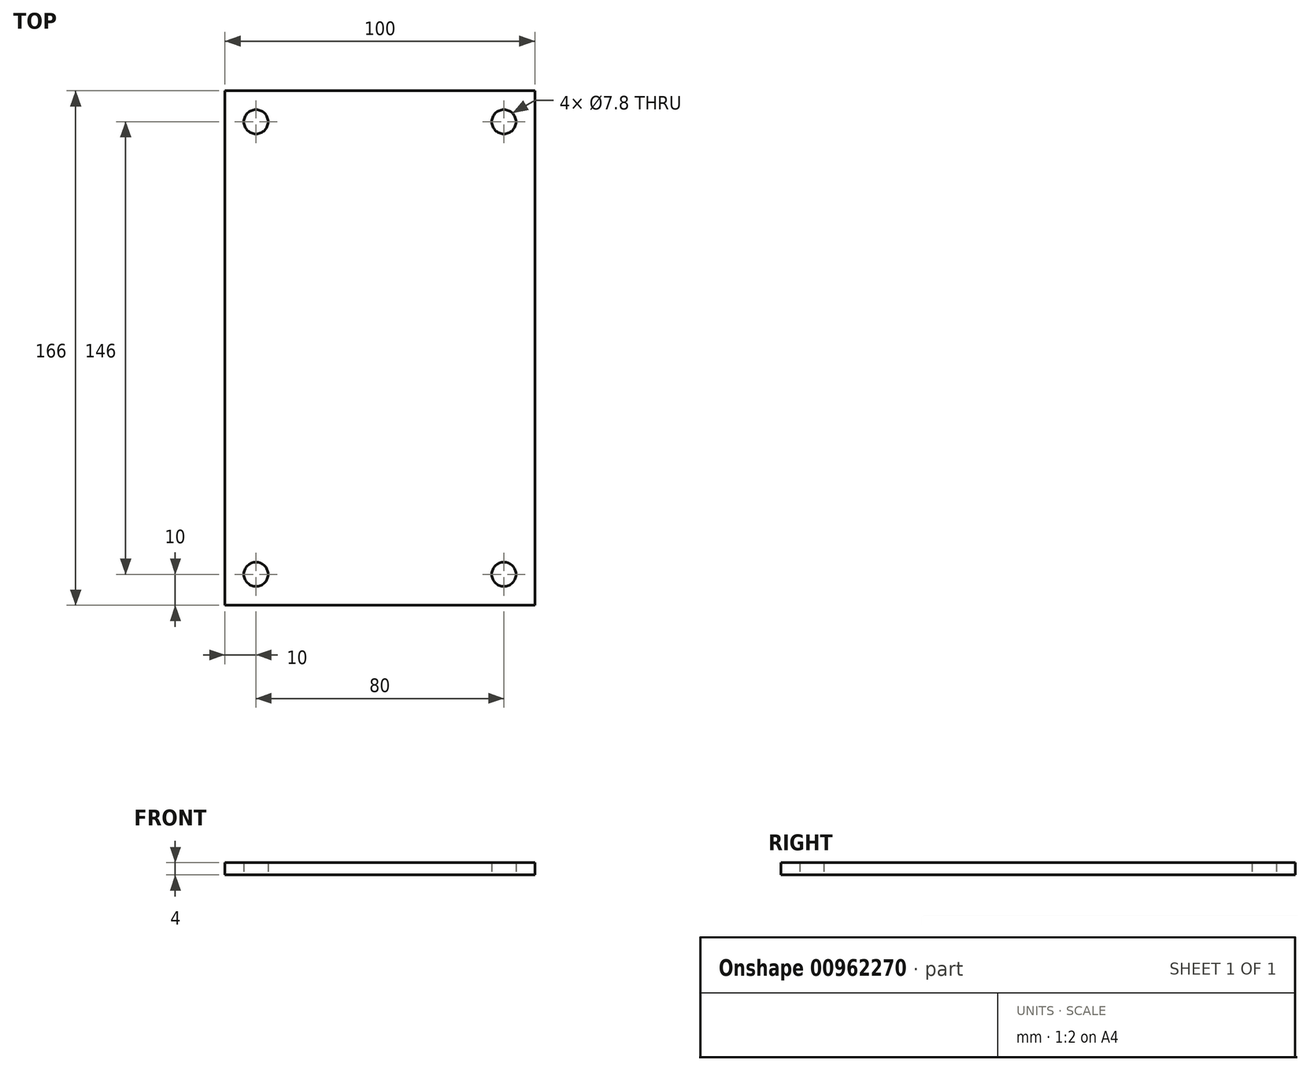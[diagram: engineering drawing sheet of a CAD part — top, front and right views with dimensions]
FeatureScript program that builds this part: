
annotation { "Feature Type Name" : "Feature", "Feature Type Description" : "" }
export const myFeature = defineFeature(function(context is Context, id is Id, definition is map)
    precondition{}
    {
        {
            var Q0;
            Q0=qCreatedBy(makeId("Top.planeOp"),FACE);
            var sketch = newSketch(context, id + "F0", { "sketchPlane" : qUnion([Q0])});
            skLineSegment(sketch, "E0.bottom", {"start": v(0, 0) * mm, "end": v(100, 0) * mm});
            skLineSegment(sketch, "E0.top", {"start": v(0, -126) * mm, "end": v(100, -126) * mm});
            skLineSegment(sketch, "E0.left", {"start": v(0, 0) * mm, "end": v(0, -126) * mm});
            skLineSegment(sketch, "E0.right", {"start": v(100, 0) * mm, "end": v(100, -126) * mm});
            skLineSegment(sketch, "E1.left", {"start": v(0, 0) * mm, "end": v(0, 0) * mm});
            skLineSegment(sketch, "E1.right", {"start": v(100, 0) * mm, "end": v(100, 0) * mm});
            skLineSegment(sketch, "E2.top", {"start": v(0, 20) * mm, "end": v(100, 20) * mm});
            skLineSegment(sketch, "E2.left", {"start": v(0, 0) * mm, "end": v(0, 20) * mm});
            skLineSegment(sketch, "E2.right", {"start": v(100, 0) * mm, "end": v(100, 20) * mm});
            skLineSegment(sketch, "E3.top", {"start": v(0, -146) * mm, "end": v(100, -146) * mm});
            skLineSegment(sketch, "E3.left", {"start": v(0, -126) * mm, "end": v(0, -146) * mm});
            skLineSegment(sketch, "E3.right", {"start": v(100, -126) * mm, "end": v(100, -146) * mm});
            skLineSegment(sketch, "E4.bottom", {"start": v(0, 20) * mm, "end": v(10, 20) * mm, "construction": true});
            skLineSegment(sketch, "E4.top", {"start": v(0, 10) * mm, "end": v(10, 10) * mm, "construction": true});
            skLineSegment(sketch, "E4.left", {"start": v(0, 20) * mm, "end": v(0, 10) * mm, "construction": true});
            skLineSegment(sketch, "E4.right", {"start": v(10, 20) * mm, "end": v(10, 10) * mm, "construction": true});
            skLineSegment(sketch, "E5.bottom", {"start": v(100, 20) * mm, "end": v(90, 20) * mm, "construction": true});
            skLineSegment(sketch, "E5.top", {"start": v(100, 10) * mm, "end": v(90, 10) * mm, "construction": true});
            skLineSegment(sketch, "E5.left", {"start": v(100, 20) * mm, "end": v(100, 10) * mm, "construction": true});
            skLineSegment(sketch, "E5.right", {"start": v(90, 20) * mm, "end": v(90, 10) * mm, "construction": true});
            skLineSegment(sketch, "E6.bottom", {"start": v(0, -146) * mm, "end": v(10, -146) * mm, "construction": true});
            skLineSegment(sketch, "E6.top", {"start": v(0, -136) * mm, "end": v(10, -136) * mm, "construction": true});
            skLineSegment(sketch, "E6.left", {"start": v(0, -146) * mm, "end": v(0, -136) * mm, "construction": true});
            skLineSegment(sketch, "E6.right", {"start": v(10, -146) * mm, "end": v(10, -136) * mm, "construction": true});
            skLineSegment(sketch, "E7.bottom", {"start": v(100, -146) * mm, "end": v(90, -146) * mm, "construction": true});
            skLineSegment(sketch, "E7.top", {"start": v(100, -136) * mm, "end": v(90, -136) * mm, "construction": true});
            skLineSegment(sketch, "E7.left", {"start": v(100, -146) * mm, "end": v(100, -136) * mm, "construction": true});
            skLineSegment(sketch, "E7.right", {"start": v(90, -146) * mm, "end": v(90, -136) * mm, "construction": true});
            skCircle(sketch, "E8", {"center": v(10, 10) * mm, "radius": 3.9 * mm});
            skCircle(sketch, "E9", {"center": v(90, 10) * mm, "radius": 3.9 * mm});
            skCircle(sketch, "E10", {"center": v(90, -136) * mm, "radius": 3.9 * mm});
            skCircle(sketch, "E11", {"center": v(10, -136) * mm, "radius": 3.9 * mm});
            skSolve(sketch);
        }
        {
            var Q0;
            Q0=makeQuery(id+"F0.imprint","IMPRINT",FACE,{"disambiguationData":[TD([[makeQuery(id+"F0.imprint","IMPRINT",EDGE,{"derivedFrom":sQuery(id+"F0.wireOp",EDGE,"E0.left")}),1.0]])]});
            var Q1;
            Q1=makeQuery(id+"F0.imprint","IMPRINT",FACE,{"disambiguationData":[TD([[makeQuery(id+"F0.imprint","IMPRINT",EDGE,{"derivedFrom":sQuery(id+"F0.wireOp",EDGE,"E0.bottom")}),1.0]])]});
            var Q2;
            Q2=makeQuery(id+"F0.imprint","IMPRINT",FACE,{"disambiguationData":[TD([[makeQuery(id+"F0.imprint","IMPRINT",EDGE,{"derivedFrom":sQuery(id+"F0.wireOp",EDGE,"E0.top")}),-1.0]])]});
            extrude(context, id + "F1", {"entities" : qUnion([Q0, Q1, Q2]), "depth" : 4 * mm, "offsetDistance" : 25 * mm});
        }
    });
